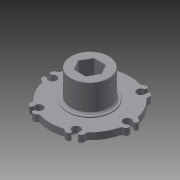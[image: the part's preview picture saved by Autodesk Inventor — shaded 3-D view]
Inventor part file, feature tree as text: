
AUTODESK INVENTOR PART (.ipt)
format: ipt  version: 2014 SP1 (Build 180222100, 222)  size: 321,024 bytes
history: native  units: in
note: dims shown in document units (in); Inventor stores cm internally (conversion verified against a paired STEP export)
features: fillet x1, other x1, imported_body x1
ambient origin geometry x8: Origin, YZ Plane, XZ Plane, XY Plane, X Axis, Y Axis, Z Axis, Center Point
bodies: Body1 (feature_tree)
feature tree (3):
  fillet  "Fillet7"  [1 undecoded]
  other  "500EX Hex Hub.ipt1"
  imported_body  "Base1"
note: 1 required parameter value undecoded (feature->parameter linkage not recoverable at this tier; creation-order binding heuristic only, values carry confidence <= 0.55)
